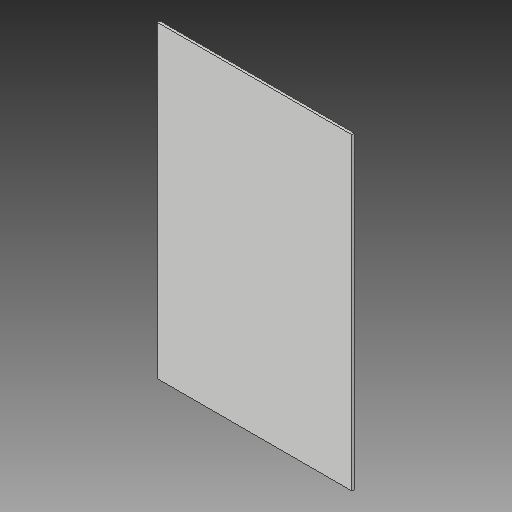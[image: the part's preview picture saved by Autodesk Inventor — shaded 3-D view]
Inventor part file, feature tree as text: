
AUTODESK INVENTOR PART (.ipt)
format: ipt  version: 2017 (Build 210142000, 142)  size: 86,016 bytes
history: native  units: in
note: dims shown in document units (in); Inventor stores cm internally (conversion verified against a paired STEP export)
features: extrude x1, sketch x1
ambient origin geometry x8: Origin, YZ Plane, XZ Plane, XY Plane, X Axis, Y Axis, Z Axis, Center Point
bodies: Solid1 (feature_tree)
feature tree (2):
  extrude  "Extrusion1"  Depth=15.086in
  sketch  "Sketch1"  dims[d0=9.5in d1=15.086in d2=0.125in d3=0.0in]
